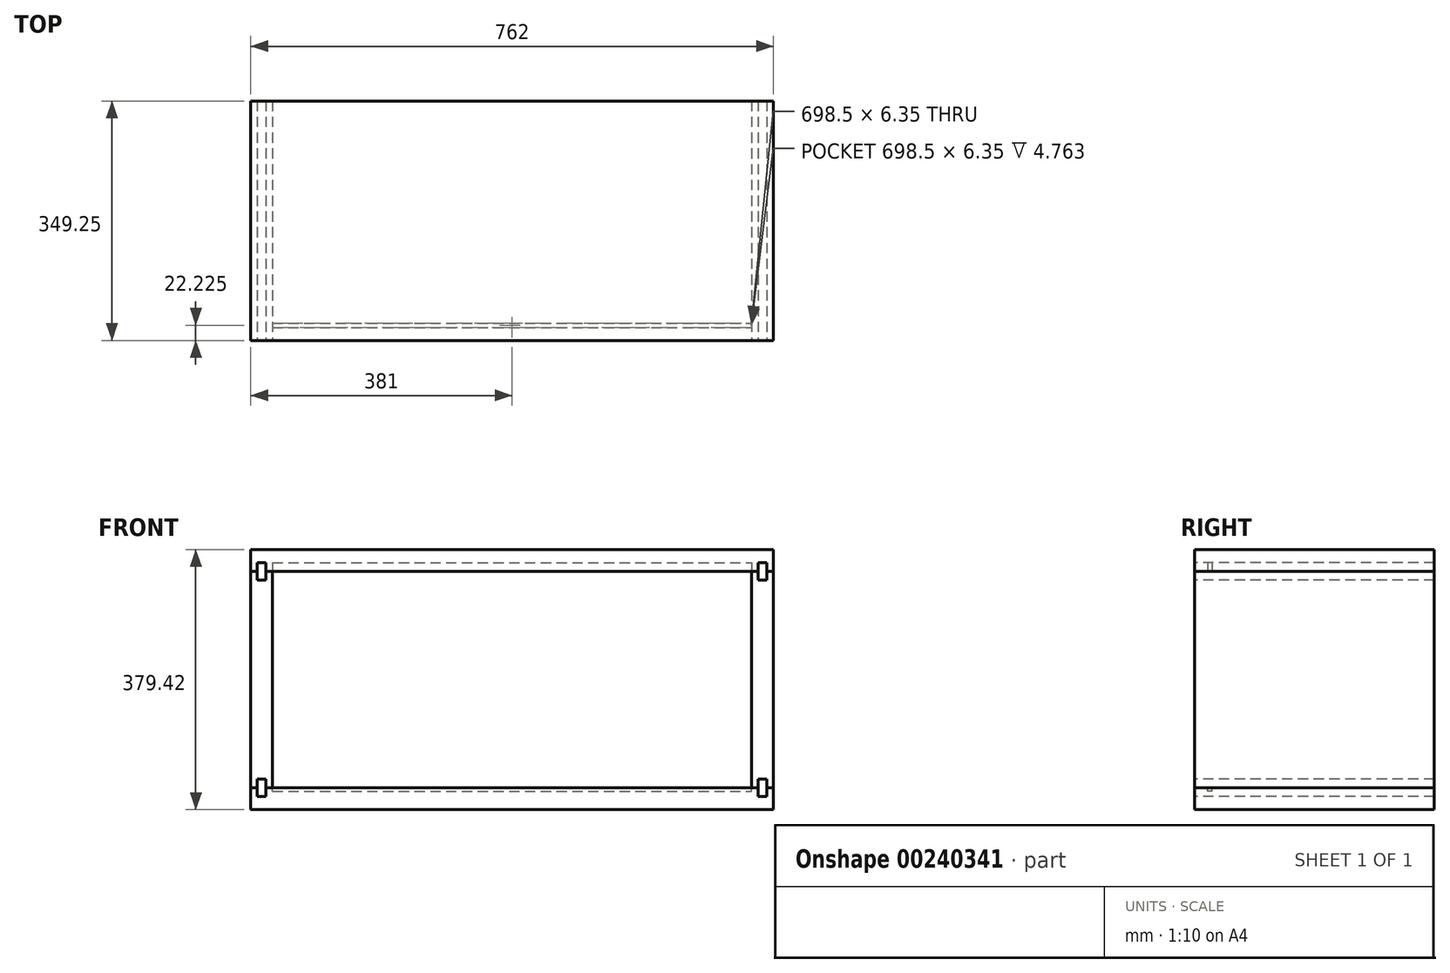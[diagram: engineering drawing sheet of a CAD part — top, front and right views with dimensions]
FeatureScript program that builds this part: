
annotation { "Feature Type Name" : "Feature", "Feature Type Description" : "" }
export const myFeature = defineFeature(function(context is Context, id is Id, definition is map)
    precondition{}
    {
        {
            var Q0;
            Q0=qCreatedBy(makeId("Front.planeOp"),FACE);
            var sketch = newSketch(context, id + "F0", { "sketchPlane" : qUnion([Q0])});
            skLineSegment(sketch, "E0.bottom", {"start": v(381, -189.7) * mm, "end": v(-381, -189.7) * mm});
            skLineSegment(sketch, "E0.top", {"start": v(381, 189.7) * mm, "end": v(-381, 189.7) * mm});
            skLineSegment(sketch, "E0.left", {"start": v(381, -189.7) * mm, "end": v(381, 189.7) * mm});
            skLineSegment(sketch, "E0.right", {"start": v(-381, -189.7) * mm, "end": v(-381, 189.7) * mm});
            skPoint(sketch, "E0.middle", {"position": v(0, 0) * mm});
            skLineSegment(sketch, "E1", {"start": v(-381, 157.96) * mm, "end": v(-371.48, 157.96) * mm});
            skLineSegment(sketch, "E2.MirrorCS", {"start": v(-381, -157.96) * mm, "end": v(-371.48, -157.96) * mm});
            skLineSegment(sketch, "E3", {"start": v(-349.25, 157.96) * mm, "end": v(-349.25, -157.96) * mm});
            skLineSegment(sketch, "E4.MirrorCS", {"start": v(349.25, 157.96) * mm, "end": v(349.25, -157.96) * mm});
            skLineSegment(sketch, "E5.bottom", {"start": v(-358.78, 145.26) * mm, "end": v(-371.48, 145.26) * mm});
            skLineSegment(sketch, "E5.top", {"start": v(-358.78, 170.66) * mm, "end": v(-371.48, 170.66) * mm});
            skLineSegment(sketch, "E5.left", {"start": v(-358.78, 145.26) * mm, "end": v(-358.78, 170.66) * mm});
            skLineSegment(sketch, "E5.right", {"start": v(-371.48, 145.26) * mm, "end": v(-371.48, 170.66) * mm});
            skPoint(sketch, "E5.middle", {"position": v(-365.13, 157.96) * mm});
            skLineSegment(sketch, "E6.trimOffspring", {"start": v(-358.78, 157.96) * mm, "end": v(358.78, 157.96) * mm});
            skPoint(sketch, "E7.MirrorP", {"position": v(365.13, 157.96) * mm});
            skLineSegment(sketch, "E8.MirrorCS", {"start": v(371.48, 145.26) * mm, "end": v(371.48, 170.66) * mm});
            skLineSegment(sketch, "E9.MirrorCS", {"start": v(358.78, 145.26) * mm, "end": v(358.78, 170.66) * mm});
            skLineSegment(sketch, "E10.MirrorCS", {"start": v(358.78, 170.66) * mm, "end": v(371.48, 170.66) * mm});
            skLineSegment(sketch, "E11.MirrorCS", {"start": v(358.78, 145.26) * mm, "end": v(371.48, 145.26) * mm});
            skLineSegment(sketch, "E12.MirrorCS", {"start": v(-358.78, -170.66) * mm, "end": v(-371.48, -170.66) * mm});
            skLineSegment(sketch, "E13.MirrorCS", {"start": v(-358.78, -145.26) * mm, "end": v(-371.48, -145.26) * mm});
            skLineSegment(sketch, "E14.MirrorCS", {"start": v(-371.48, -145.26) * mm, "end": v(-371.48, -170.66) * mm});
            skLineSegment(sketch, "E15.MirrorCS", {"start": v(-358.78, -145.26) * mm, "end": v(-358.78, -170.66) * mm});
            skPoint(sketch, "E16.MirrorP", {"position": v(-365.13, -157.96) * mm});
            skLineSegment(sketch, "E17.MirrorCS", {"start": v(358.78, -145.26) * mm, "end": v(371.48, -145.26) * mm});
            skLineSegment(sketch, "E18.MirrorCS", {"start": v(358.78, -170.66) * mm, "end": v(371.48, -170.66) * mm});
            skLineSegment(sketch, "E19.MirrorCS", {"start": v(358.78, -145.26) * mm, "end": v(358.78, -170.66) * mm});
            skLineSegment(sketch, "E20.MirrorCS", {"start": v(371.48, -145.26) * mm, "end": v(371.48, -170.66) * mm});
            skPoint(sketch, "E21.MirrorP", {"position": v(365.13, -157.96) * mm});
            skLineSegment(sketch, "E22.trimOffspring", {"start": v(-358.78, -157.96) * mm, "end": v(358.78, -157.96) * mm});
            skLineSegment(sketch, "E23.trimOffspring", {"start": v(371.48, -157.96) * mm, "end": v(381, -157.96) * mm});
            skLineSegment(sketch, "E24.trimOffspring", {"start": v(371.48, 157.96) * mm, "end": v(381, 157.96) * mm});
            skLineSegment(sketch, "E25", {"start": v(-371.48, 170.66) * mm, "end": v(-358.78, 170.66) * mm});
            skLineSegment(sketch, "E26", {"start": v(-371.48, 145.26) * mm, "end": v(-358.78, 145.26) * mm});
            skSolve(sketch);
        }
        {
            var Q0;
            {var subQ14=sQuery(id+"F0.wireOp",EDGE,"E0.top");Q0=makeQuery(id+"F0.imprint","IMPRINT",FACE,{"disambiguationData":[TD([[makeQuery(id+"F0.imprint","IMPRINT",EDGE,{"derivedFrom":subQ14}),1.0]])]});}
            extrude(context, id + "F1", {"entities" : qUnion([Q0]), "oppositeDirection" : true, "depth" : 349.25 * mm});
        }
        {
            var Q0;
            {var subQ6=sQuery(id+"F0.wireOp",EDGE,"E1");Q0=makeQuery(id+"F0.imprint","IMPRINT",FACE,{"disambiguationData":[TD([[makeQuery(id+"F0.imprint","IMPRINT",EDGE,{"derivedFrom":subQ6}),-1.0]])]});}
            extrude(context, id + "F2", {"entities" : qUnion([Q0]), "oppositeDirection" : true, "depth" : 349.25 * mm});
        }
        {
            var Q0;
            Q0=makeQuery(id+"F1.opExtrude","SWEPT_BODY",BODY,{"disambiguationData":[OSD([sQuery(id+"F0.wireOp",EDGE,"E0.top"),sQuery(id+"F0.wireOp",EDGE,"E0.left"),sQuery(id+"F0.wireOp",EDGE,"E0.right"),sQuery(id+"F0.wireOp",EDGE,"E1"),sQuery(id+"F0.wireOp",EDGE,"E5.top"),sQuery(id+"F0.wireOp",EDGE,"E5.left"),sQuery(id+"F0.wireOp",EDGE,"E5.right"),sQuery(id+"F0.wireOp",EDGE,"E6.trimOffspring"),sQuery(id+"F0.wireOp",EDGE,"E8.MirrorCS"),sQuery(id+"F0.wireOp",EDGE,"E9.MirrorCS"),sQuery(id+"F0.wireOp",EDGE,"E10.MirrorCS"),sQuery(id+"F0.wireOp",EDGE,"E24.trimOffspring")])]});
            var Q1;
            Q1=makeQuery(id+"F2.opExtrude","SWEPT_BODY",BODY,{"disambiguationData":[OSD([sQuery(id+"F0.wireOp",EDGE,"E0.right"),sQuery(id+"F0.wireOp",EDGE,"E1"),sQuery(id+"F0.wireOp",EDGE,"E2.MirrorCS"),sQuery(id+"F0.wireOp",EDGE,"E3"),sQuery(id+"F0.wireOp",EDGE,"E5.bottom"),sQuery(id+"F0.wireOp",EDGE,"E5.left"),sQuery(id+"F0.wireOp",EDGE,"E5.right"),sQuery(id+"F0.wireOp",EDGE,"E6.trimOffspring"),sQuery(id+"F0.wireOp",EDGE,"E13.MirrorCS"),sQuery(id+"F0.wireOp",EDGE,"E14.MirrorCS"),sQuery(id+"F0.wireOp",EDGE,"E15.MirrorCS"),sQuery(id+"F0.wireOp",EDGE,"E22.trimOffspring")])]});
            var Q2;
            Q2=qCreatedBy(makeId("Top.planeOp"),FACE);
            mirror(context, id + "F3", {"entities" : qUnion([Q0, Q1]), "mirrorPlane" : qUnion([Q2])});
        }
        {
            var Q0;
            Q0=makeQuery(id+"F2.opExtrude","SWEPT_BODY",BODY,{"disambiguationData":[OSD([sQuery(id+"F0.wireOp",EDGE,"E0.right"),sQuery(id+"F0.wireOp",EDGE,"E1"),sQuery(id+"F0.wireOp",EDGE,"E2.MirrorCS"),sQuery(id+"F0.wireOp",EDGE,"E3"),sQuery(id+"F0.wireOp",EDGE,"E5.bottom"),sQuery(id+"F0.wireOp",EDGE,"E5.left"),sQuery(id+"F0.wireOp",EDGE,"E5.right"),sQuery(id+"F0.wireOp",EDGE,"E6.trimOffspring"),sQuery(id+"F0.wireOp",EDGE,"E13.MirrorCS"),sQuery(id+"F0.wireOp",EDGE,"E14.MirrorCS"),sQuery(id+"F0.wireOp",EDGE,"E15.MirrorCS"),sQuery(id+"F0.wireOp",EDGE,"E22.trimOffspring")])]});
            var Q1;
            Q1=makeQuery(id+"F5BdRq8yITpkPnx_3.opExtrude","SWEPT_BODY",BODY,{"disambiguationData":[OSD([sQuery(id+"F0.wireOp",EDGE,"E5.left"),sQuery(id+"F0.wireOp",EDGE,"E5.right"),sQuery(id+"F0.wireOp",EDGE,"tNECQNf6-u9PO-y4OO-61F0-2PMgRv8fRv7j"),sQuery(id+"F0.wireOp",EDGE,"4H5L6nFQ-Hccq-sgf2-1u0k-HYD7SNM5MLTO")])]});
            var Q2;
            Q2=makeQuery(id+"FO8Gd2ggb04Vu7J_4.opPattern","COPY",BODY,{"derivedFrom":makeQuery(id+"F5BdRq8yITpkPnx_3.opExtrude","SWEPT_BODY",BODY,{"disambiguationData":[OSD([sQuery(id+"F0.wireOp",EDGE,"E5.left"),sQuery(id+"F0.wireOp",EDGE,"E5.right"),sQuery(id+"F0.wireOp",EDGE,"tNECQNf6-u9PO-y4OO-61F0-2PMgRv8fRv7j"),sQuery(id+"F0.wireOp",EDGE,"4H5L6nFQ-Hccq-sgf2-1u0k-HYD7SNM5MLTO")])]}),"instanceName":"1"});
            var Q3;
            Q3=qCreatedBy(makeId("Right.planeOp"),FACE);
            mirror(context, id + "F4", {"entities" : qUnion([Q0, Q1, Q2]), "mirrorPlane" : qUnion([Q3])});
        }
        {
            var Q0;
            Q0=makeQuery(id+"F3.opPattern","COPY",FACE,{"derivedFrom":makeQuery(id+"F1.opExtrude","SWEPT_FACE",FACE,{"disambiguationData":[OSD([sQuery(id+"F0.wireOp",EDGE,"E6.trimOffspring")])]}),"instanceName":"1"});
            var sketch = newSketch(context, id + "F5", { "sketchPlane" : qUnion([Q0])});
            skLineSegment(sketch, "E27.0", {"start": v(-349.25, 25.4) * mm, "end": v(-349.25, 19.05) * mm});
            skLineSegment(sketch, "E28.0", {"start": v(349.25, 25.4) * mm, "end": v(349.25, 19.05) * mm});
            skLineSegment(sketch, "E29.0", {"start": v(-349.25, 19.05) * mm, "end": v(361.95, 19.05) * mm});
            skLineSegment(sketch, "E30", {"start": v(-349.25, 25.4) * mm, "end": v(349.25, 25.4) * mm});
            skPoint(sketch, "E31.orphan", {"position": v(-349.25, 349.25) * mm});
            skPoint(sketch, "E32.orphan", {"position": v(-349.25, 0) * mm});
            skPoint(sketch, "E33.orphan", {"position": v(349.25, 349.25) * mm});
            skPoint(sketch, "E34.orphan", {"position": v(349.25, 0) * mm});
            skSolve(sketch);
        }
        {
            var Q0;
            Q0 = qSketchRegion(id + "F5", true);
            extrude(context, id + "F6", {"entities" : qUnion([Q0]), "operationType" : NewBodyOperationType.REMOVE, "oppositeDirection" : true, "depth" : 4.76 * mm});
        }
        {
            var Q0;
            Q0=makeQuery(id+"F1.opExtrude","SWEPT_FACE",FACE,{"disambiguationData":[OSD([sQuery(id+"F0.wireOp",EDGE,"E6.trimOffspring")])]});
            var sketch = newSketch(context, id + "F7", { "sketchPlane" : qUnion([Q0])});
            skLineSegment(sketch, "E35.0", {"start": v(-349.25, -25.4) * mm, "end": v(-349.25, -19.05) * mm});
            skLineSegment(sketch, "E36.0", {"start": v(349.25, -25.4) * mm, "end": v(349.25, -19.05) * mm});
            skLineSegment(sketch, "E37.0", {"start": v(-358.78, -19.05) * mm, "end": v(358.78, -19.05) * mm});
            skLineSegment(sketch, "E38", {"start": v(-349.25, -25.4) * mm, "end": v(349.25, -25.4) * mm});
            skPoint(sketch, "E39.orphan", {"position": v(349.25, 0) * mm});
            skPoint(sketch, "E40.orphan", {"position": v(349.25, -349.25) * mm});
            skPoint(sketch, "E41.orphan", {"position": v(-349.25, 0) * mm});
            skPoint(sketch, "E42.orphan", {"position": v(-349.25, -349.25) * mm});
            skSolve(sketch);
        }
        {
            var Q0;
            Q0 = qSketchRegion(id + "F7", true);
            extrude(context, id + "F8", {"entities" : qUnion([Q0]), "operationType" : NewBodyOperationType.REMOVE, "oppositeDirection" : true, "depth" : 12.7 * mm});
        }
        {
            var Q0;
            {var subQ14=sQuery(id+"F0.wireOp",EDGE,"E0.top");Q0=makeQuery(id+"F0.imprint","IMPRINT",FACE,{"disambiguationData":[TD([[makeQuery(id+"F0.imprint","IMPRINT",EDGE,{"derivedFrom":subQ14}),1.0]])]});}
            var sketch = newSketch(context, id + "F9", { "sketchPlane" : qUnion([Q0])});
            skLineSegment(sketch, "E43.0.0", {"start": v(-371.48, 157.96) * mm, "end": v(-371.48, 145.26) * mm});
            skLineSegment(sketch, "E43.0.1", {"start": v(-371.48, 145.26) * mm, "end": v(-358.78, 145.26) * mm});
            skLineSegment(sketch, "E43.0.2", {"start": v(-358.78, 145.26) * mm, "end": v(-358.78, 157.96) * mm});
            skLineSegment(sketch, "E43.0.3", {"start": v(-358.78, 157.96) * mm, "end": v(-358.78, 170.66) * mm});
            skLineSegment(sketch, "E43.0.4", {"start": v(-358.78, 170.66) * mm, "end": v(-371.48, 170.66) * mm});
            skLineSegment(sketch, "E43.0.5", {"start": v(-371.48, 170.66) * mm, "end": v(-371.48, 157.96) * mm});
            skSolve(sketch);
        }
        {
            var Q0;
            Q0 = qSketchRegion(id + "F9", true);
            var Q1;
            Q1=makeQuery(id+"F2.opExtrude","CAP_FACE",FACE,{"disambiguationData":[OSD([sQuery(id+"F0.wireOp",EDGE,"E0.right"),sQuery(id+"F0.wireOp",EDGE,"E1"),sQuery(id+"F0.wireOp",EDGE,"E2.MirrorCS"),sQuery(id+"F0.wireOp",EDGE,"E3"),sQuery(id+"F0.wireOp",EDGE,"E5.left"),sQuery(id+"F0.wireOp",EDGE,"E5.right"),sQuery(id+"F0.wireOp",EDGE,"E6.trimOffspring"),sQuery(id+"F0.wireOp",EDGE,"E13.MirrorCS"),sQuery(id+"F0.wireOp",EDGE,"E14.MirrorCS"),sQuery(id+"F0.wireOp",EDGE,"E15.MirrorCS"),sQuery(id+"F0.wireOp",EDGE,"E22.trimOffspring"),sQuery(id+"F0.wireOp",EDGE,"E26")])],"isStart":false});
            extrude(context, id + "F10", {"entities" : qUnion([Q0]), "endBound" : BoundingType.UP_TO_SURFACE, "oppositeDirection" : true, "endBoundEntityFace" : qUnion([Q1]), "depth" : 25.4 * mm});
        }
        {
            var Q0;
            Q0=makeQuery(id+"F10.opExtrude","SWEPT_BODY",BODY,{"disambiguationData":[OSD([sQuery(id+"F9.wireOp",EDGE,"E43.0.0"),sQuery(id+"F9.wireOp",EDGE,"E43.0.1"),sQuery(id+"F9.wireOp",EDGE,"E43.0.2"),sQuery(id+"F9.wireOp",EDGE,"E43.0.3"),sQuery(id+"F9.wireOp",EDGE,"E43.0.4"),sQuery(id+"F9.wireOp",EDGE,"E43.0.5")])]});
            var Q1;
            Q1=qCreatedBy(makeId("Right.planeOp"),FACE);
            mirror(context, id + "F11", {"entities" : qUnion([Q0]), "mirrorPlane" : qUnion([Q1])});
        }
        {
            var Q0;
            Q0=makeQuery(id+"F10.opExtrude","SWEPT_BODY",BODY,{"disambiguationData":[OSD([sQuery(id+"F9.wireOp",EDGE,"E43.0.0"),sQuery(id+"F9.wireOp",EDGE,"E43.0.1"),sQuery(id+"F9.wireOp",EDGE,"E43.0.2"),sQuery(id+"F9.wireOp",EDGE,"E43.0.3"),sQuery(id+"F9.wireOp",EDGE,"E43.0.4"),sQuery(id+"F9.wireOp",EDGE,"E43.0.5")])]});
            var Q1;
            Q1=makeQuery(id+"F11.opPattern","COPY",BODY,{"derivedFrom":makeQuery(id+"F10.opExtrude","SWEPT_BODY",BODY,{"disambiguationData":[OSD([sQuery(id+"F9.wireOp",EDGE,"E43.0.0"),sQuery(id+"F9.wireOp",EDGE,"E43.0.1"),sQuery(id+"F9.wireOp",EDGE,"E43.0.2"),sQuery(id+"F9.wireOp",EDGE,"E43.0.3"),sQuery(id+"F9.wireOp",EDGE,"E43.0.4"),sQuery(id+"F9.wireOp",EDGE,"E43.0.5")])]}),"instanceName":"1"});
            var Q2;
            Q2=qCreatedBy(makeId("Top.planeOp"),FACE);
            mirror(context, id + "F12", {"entities" : qUnion([Q0, Q1]), "mirrorPlane" : qUnion([Q2])});
        }
        {
            var Q0;
            Q0=makeQuery(id+"F2.opExtrude","SWEPT_BODY",BODY,{"disambiguationData":[OSD([sQuery(id+"F0.wireOp",EDGE,"E0.right"),sQuery(id+"F0.wireOp",EDGE,"E1"),sQuery(id+"F0.wireOp",EDGE,"E2.MirrorCS"),sQuery(id+"F0.wireOp",EDGE,"E3"),sQuery(id+"F0.wireOp",EDGE,"E5.left"),sQuery(id+"F0.wireOp",EDGE,"E5.right"),sQuery(id+"F0.wireOp",EDGE,"E6.trimOffspring"),sQuery(id+"F0.wireOp",EDGE,"E13.MirrorCS"),sQuery(id+"F0.wireOp",EDGE,"E14.MirrorCS"),sQuery(id+"F0.wireOp",EDGE,"E15.MirrorCS"),sQuery(id+"F0.wireOp",EDGE,"E22.trimOffspring"),sQuery(id+"F0.wireOp",EDGE,"E26")])]});
            deleteBodies(context, id + "F13", {"entities" : qUnion([Q0])});
        }
    });
